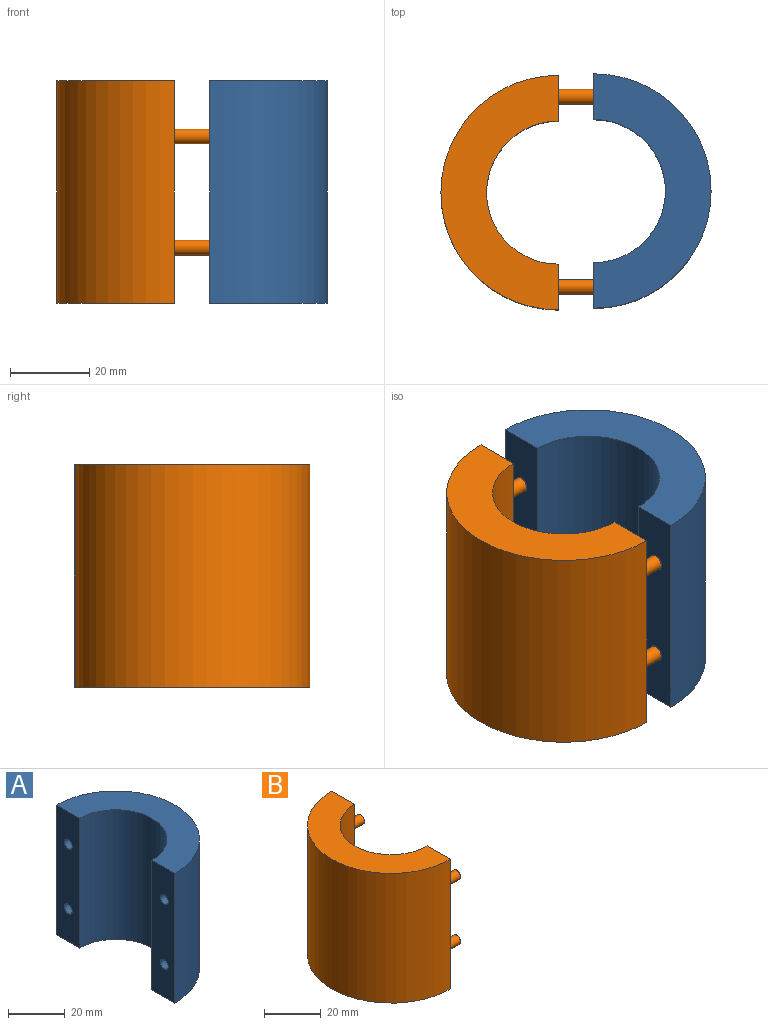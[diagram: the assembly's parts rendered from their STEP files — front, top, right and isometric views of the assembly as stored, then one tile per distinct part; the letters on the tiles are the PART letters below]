
ASSEMBLY  parts=2 mates=1
PART A: 14 faces, bbox 29.5x59x56 mm
  f0: cylinder r=18mm len=56mm, axis (0,0,-1), area 3166.7mm2, adj f2,f3,f4,f5
  f1: cylinder r=29.5mm len=59mm, axis (0,0,-1), area 5189.9mm2, adj f2,f3,f4,f5
  f2: plane 59x29.5mm, normal (0,0,1), area 858mm2, adj f0,f1,f4,f5
  f3: plane 59x29.5mm, normal (0,0,-1), area 858mm2, adj f0,f1,f4,f5
  f4: plane 56x11.5mm, normal (-1,0,0), area 618.9mm2, adj f0,f1,f2,f3,f11,f13
  f5: plane 56x11.5mm, normal (-1,0,0), area 618.9mm2, adj f0,f1,f2,f3,f7,f9
  f6: cone r=0mm half-angle=59deg, axis (-1,0,0), area 14.7mm2, adj f7
  f7: cylinder r=2mm len=10mm, axis (-1,0,0), area 125.7mm2, adj f5,f6
  f8: cone r=0mm half-angle=59deg, axis (-1,0,0), area 14.7mm2, adj f9
  f9: cylinder r=2mm len=10mm, axis (-1,0,0), area 125.7mm2, adj f5,f8
  f10: cone r=0mm half-angle=59deg, axis (-1,0,0), area 14.7mm2, adj f11
  f11: cylinder r=2mm len=10mm, axis (-1,0,0), area 125.7mm2, adj f4,f10
  f12: cone r=0mm half-angle=59deg, axis (-1,0,0), area 14.7mm2, adj f13
  f13: cylinder r=2mm len=10mm, axis (-1,0,0), area 125.7mm2, adj f4,f12
PART B: 14 faces, bbox 38.5x59x56 mm
  f0: plane 56x11.5mm, normal (1,0,0), area 621.9mm2, adj f1,f2,f3,f4,f6,f8
  f1: plane 59x29.5mm, normal (0,0,-1), area 858mm2, adj f0,f3,f4,f5
  f2: plane 59x29.5mm, normal (0,0,1), area 858mm2, adj f0,f3,f4,f5
  f3: cylinder r=29.5mm len=59mm, axis (0,0,-1), area 5189.9mm2, adj f0,f1,f2,f5
  f4: cylinder r=18mm len=56mm, axis (0,0,-1), area 3166.7mm2, adj f0,f1,f2,f5
  f5: plane 56x11.5mm, normal (1,0,0), area 621.9mm2, adj f1,f2,f3,f4,f10,f12
  f6: cylinder r=1.88mm len=9mm, axis (-1,0,0), area 106mm2, adj f0,f7
  f7: plane 3.75x3.75mm, normal (1,0,0), area 11mm2, adj f6
  f8: cylinder r=1.88mm len=9mm, axis (-1,0,0), area 106mm2, adj f0,f9
  f9: plane 3.75x3.75mm, normal (1,0,0), area 11mm2, adj f8
  f10: cylinder r=1.88mm len=9mm, axis (-1,0,0), area 106mm2, adj f5,f11
  f11: plane 3.75x3.75mm, normal (1,0,0), area 11mm2, adj f10
  f12: cylinder r=1.88mm len=9mm, axis (-1,0,0), area 106mm2, adj f5,f13
  f13: plane 3.75x3.75mm, normal (1,0,0), area 11mm2, adj f12
PLACE A t=(9,0.39,0)mm
PLACE B at identity
MATE pin_slot A.f10 <-> B.f12  axis (-1,0,0) through (9,24.14,14)mm
